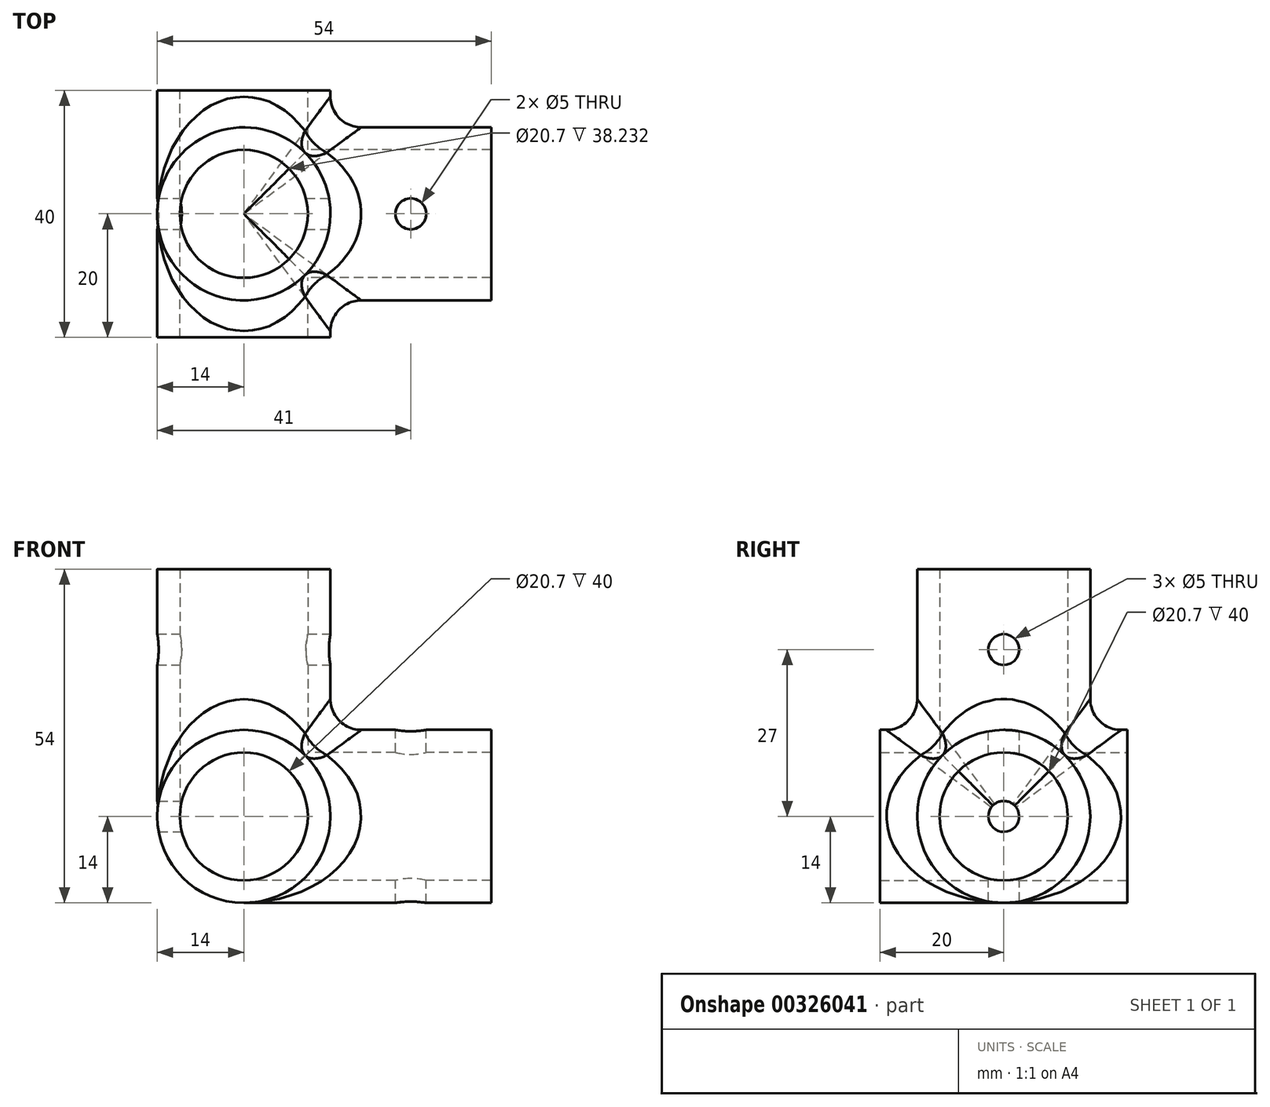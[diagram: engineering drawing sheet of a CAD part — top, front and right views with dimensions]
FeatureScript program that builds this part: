
annotation { "Feature Type Name" : "Feature", "Feature Type Description" : "" }
export const myFeature = defineFeature(function(context is Context, id is Id, definition is map)
    precondition{}
    {
        {
            var Q0;
            Q0=qCreatedBy(makeId("Front.planeOp"),FACE);
            var sketch = newSketch(context, id + "F0", { "sketchPlane" : qUnion([Q0])});
            skCircle(sketch, "E0", {"center": v(0, 0) * mm, "radius": 14 * mm});
            skSolve(sketch);
        }
        {
            var Q0;
            Q0=makeQuery(id+"F0.imprint","IMPRINT",FACE,{"disambiguationData":[TD([[makeQuery(id+"F0.imprint","IMPRINT",EDGE,{"derivedFrom":sQuery(id+"F0.wireOp",EDGE,"E0")}),1.0]])]});
            extrude(context, id + "F1", {"entities" : qUnion([Q0]), "depth" : 20 * mm, "hasSecondDirection" : true, "secondDirectionOppositeDirection" : true, "secondDirectionDepth" : 20 * mm});
        }
        {
            var Q0;
            Q0=qCreatedBy(makeId("Top.planeOp"),FACE);
            var sketch = newSketch(context, id + "F2", { "sketchPlane" : qUnion([Q0])});
            skCircle(sketch, "E1", {"center": v(0, 0) * mm, "radius": 14 * mm});
            skSolve(sketch);
        }
        {
            var Q0;
            Q0=makeQuery(id+"F2.imprint","IMPRINT",FACE,{"disambiguationData":[TD([[makeQuery(id+"F2.imprint","IMPRINT",EDGE,{"derivedFrom":sQuery(id+"F2.wireOp",EDGE,"E1")}),1.0]])]});
            extrude(context, id + "F3", {"entities" : qUnion([Q0]), "operationType" : NewBodyOperationType.ADD, "depth" : 40 * mm});
        }
        {
            var Q0;
            Q0=qCreatedBy(makeId("Right.planeOp"),FACE);
            var sketch = newSketch(context, id + "F4", { "sketchPlane" : qUnion([Q0])});
            skPoint(sketch, "E2.0", {"position": v(0, -14) * mm});
            skCircle(sketch, "E3", {"center": v(0, 0) * mm, "radius": 14 * mm});
            skSolve(sketch);
        }
        {
            var Q0;
            Q0=makeQuery(id+"F4.imprint","IMPRINT",FACE,{"disambiguationData":[TD([[makeQuery(id+"F4.imprint","IMPRINT",EDGE,{"derivedFrom":sQuery(id+"F4.wireOp",EDGE,"E3")}),1.0]])]});
            extrude(context, id + "F5", {"entities" : qUnion([Q0]), "operationType" : NewBodyOperationType.ADD, "depth" : 40 * mm});
        }
        {
            var Q0;
            Q0=makeQuery(id+"F1.opExtrude","CAP_FACE",FACE,{"disambiguationData":[OSD([sQuery(id+"F0.wireOp",EDGE,"E0")])],"isStart":false});
            var sketch = newSketch(context, id + "F6", { "sketchPlane" : qUnion([Q0])});
            skPoint(sketch, "E4.0", {"position": v(0, 0) * mm});
            skSolve(sketch);
        }
        {
            var Q0;
            Q0=makeQuery(id+"F3.opExtrude","CAP_FACE",FACE,{"disambiguationData":[OSD([sQuery(id+"F2.wireOp",EDGE,"E1")])],"isStart":false});
            var sketch = newSketch(context, id + "F7", { "sketchPlane" : qUnion([Q0])});
            skPoint(sketch, "E5.0", {"position": v(0, 0) * mm});
            skSolve(sketch);
        }
        {
            var Q0;
            Q0=makeQuery(id+"F5.opExtrude","CAP_FACE",FACE,{"disambiguationData":[OSD([sQuery(id+"F4.wireOp",EDGE,"E3")])],"isStart":false});
            var sketch = newSketch(context, id + "F8", { "sketchPlane" : qUnion([Q0])});
            skPoint(sketch, "E6.0", {"position": v(0, 0) * mm});
            skSolve(sketch);
        }
        {
            var Q0;
            Q0=sQuery(id+"F8.wireOp",VERTEX,"E6.0");
            var Q1;
            Q1=sQuery(id+"F6.wireOp",VERTEX,"E4.0");
            var Q2;
            Q2=sQuery(id+"F7.wireOp",VERTEX,"E5.0");
            var Q3;
            Q3=makeQuery(id+"F1.opExtrude","SWEPT_BODY",BODY,{"disambiguationData":[OSD([sQuery(id+"F0.wireOp",EDGE,"E0")])]});
            hole(context, id + "F9", {"style" : HoleStyle.SIMPLE, "endStyle" : HoleEndStyle.BLIND, "holeDiameter" : 20.7 * mm, "holeDepth" : 40 * mm, "tappedDepth" : 12 * mm, "tapClearance" : 3, "locations" : qUnion([Q0, Q1, Q2]), "scope" : qUnion([Q3]), "startStyle" : HoleStartStyle.PART});
        }
        {
            var Q0;
            Q0=makeQuery(id+"F5.boolean.opBoolean","INTERSECT",EDGE,{"derivedFrom":[makeQuery(id+"F3.opExtrude","SWEPT_FACE",FACE,{"disambiguationData":[OSD([sQuery(id+"F2.wireOp",EDGE,"E1")])]}),makeQuery(id+"F5.opExtrude","SWEPT_FACE",FACE,{"disambiguationData":[OSD([sQuery(id+"F4.wireOp",EDGE,"E3")])]})]});
            var Q1;
            Q1=makeQuery(id+"F5.boolean.opBoolean","INTERSECT",EDGE,{"derivedFrom":[makeQuery(id+"F1.opExtrude","SWEPT_FACE",FACE,{"disambiguationData":[OSD([sQuery(id+"F0.wireOp",EDGE,"E0")])]}),makeQuery(id+"F5.opExtrude","SWEPT_FACE",FACE,{"disambiguationData":[OSD([sQuery(id+"F4.wireOp",EDGE,"E3")])]})]});
            var Q2;
            Q2=makeQuery(id+"F3.boolean.opBoolean","INTERSECT",EDGE,{"derivedFrom":[makeQuery(id+"F1.opExtrude","SWEPT_FACE",FACE,{"disambiguationData":[OSD([sQuery(id+"F0.wireOp",EDGE,"E0")])]}),makeQuery(id+"F3.opExtrude","SWEPT_FACE",FACE,{"disambiguationData":[OSD([sQuery(id+"F2.wireOp",EDGE,"E1")])]})]});
            fillet(context, id + "F10", {"entities" : qUnion([Q0, Q1, Q2]), "radius" : 5 * mm, "tangentPropagation" : true, "allowEdgeOverflow" : false});
        }
        {
            var Q0;
            Q0=qCreatedBy(makeId("Right.planeOp"),FACE);
            cPlane(context, id + "F11", {"entities" : qUnion([Q0]), "cplaneType" : CPlaneType.OFFSET, "offset" : 25 * mm, "oppositeDirection" : true, "width" : 150 * mm, "height" : 150 * mm});
        }
        {
            var Q0;
            Q0=qCreatedBy(id+"F11.planeOp",FACE);
            var sketch = newSketch(context, id + "F12", { "sketchPlane" : qUnion([Q0])});
            skLineSegment(sketch, "E7.0", {"start": v(-14, 40) * mm, "end": v(14, 40) * mm});
            skLineSegment(sketch, "E8.0", {"start": v(-20, -14) * mm, "end": v(-20, 14) * mm});
            skPoint(sketch, "E9", {"position": v(0, 27) * mm});
            skPoint(sketch, "E9.positionSnap0", {"position": v(0, 40) * mm});
            skPoint(sketch, "E10", {"position": v(0, 0) * mm});
            skPoint(sketch, "E10.positionSnap0", {"position": v(-20, 0) * mm});
            skCircle(sketch, "E11.0", {"center": v(0, 0) * mm, "radius": 14 * mm, "construction": true});
            skLineSegment(sketch, "E12", {"start": v(0, 40) * mm, "end": v(0, 14) * mm, "construction": true});
            skSolve(sketch);
        }
        {
            var Q0;
            Q0=qCreatedBy(makeId("Top.planeOp"),FACE);
            cPlane(context, id + "F13", {"entities" : qUnion([Q0]), "cplaneType" : CPlaneType.OFFSET, "offset" : 25 * mm, "oppositeDirection" : true, "width" : 150 * mm, "height" : 150 * mm});
        }
        {
            var Q0;
            Q0=qCreatedBy(id+"F13.planeOp",FACE);
            var sketch = newSketch(context, id + "F14", { "sketchPlane" : qUnion([Q0])});
            skLineSegment(sketch, "E13.0", {"start": v(40, 14) * mm, "end": v(40, -14) * mm});
            skPoint(sketch, "E14", {"position": v(27, 0) * mm});
            skPoint(sketch, "E14.positionSnap0", {"position": v(40, 0) * mm});
            skLineSegment(sketch, "E15.0", {"start": v(14, 20) * mm, "end": v(-14, 20) * mm, "construction": true});
            skLineSegment(sketch, "E16", {"start": v(-14, -20) * mm, "end": v(-14, 20) * mm, "construction": true});
            skLineSegment(sketch, "E17.0", {"start": v(14, -20) * mm, "end": v(-14, -20) * mm, "construction": true});
            skLineSegment(sketch, "E18", {"start": v(14, 20) * mm, "end": v(14, -20) * mm, "construction": true});
            skLineSegment(sketch, "E19", {"start": v(40, 0) * mm, "end": v(14, 0) * mm, "construction": true});
            skSolve(sketch);
        }
        {
            var Q0;
            Q0=sQuery(id+"F14.wireOp",VERTEX,"E14");
            var Q1;
            Q1=sQuery(id+"F12.wireOp",VERTEX,"E9");
            var Q2;
            Q2=sQuery(id+"F12.wireOp",VERTEX,"E10");
            var Q3;
            Q3=makeQuery(id+"F1.opExtrude","SWEPT_BODY",BODY,{"disambiguationData":[OSD([sQuery(id+"F0.wireOp",EDGE,"E0")])]});
            hole(context, id + "F15", {"style" : HoleStyle.SIMPLE, "endStyle" : HoleEndStyle.BLIND, "oppositeDirection" : true, "holeDiameter" : 5 * mm, "holeDepth" : 30 * mm, "tappedDepth" : 12 * mm, "tapClearance" : 3, "locations" : qUnion([Q0, Q1, Q2]), "scope" : qUnion([Q3]), "startStyle" : HoleStartStyle.PART});
        }
    });
